# Revit family: 45120183
name_source: partatom
category: Plumbing Fixtures
revit_build: Autodesk Revit 2018 (Build: 20170223_1515(x64)
units: mm (PartAtom-declared; Revit-internal decimal feet)

## family parameters
Always vertical = Yes
Cut with Voids When Loaded = No
OmniClass Number = 23.45.55.00
OmniClass Title = Sanitary Faucets, Wastes
Part Type = Normal
Room Calculation Point = No
Round Connector Dimension = Use Diameter
Shared = No
Work Plane-Based = No

## types (1)
- 45120183 Shower faucet
    2D/3D/BIM Files URL = http://static.hansa.com
    3D View = https://static.hansa.com
    Additional Features = protected against back-flow in domestic use (according to DIN EN 1717)
    Advanced Features = Inner body made of DZR brass
    Approval DVGW = DW-6506CS0561
    Approval KIWA = K6116/08
    AssetType = Fixed
    BIMObjectName = 45120183
    Backflow Prevention EN1717 = EB
    BodyMaterial = Brass
    Brand = HANSA
    Catalog Drawing URL = http://static.hansa.com
    Category = Bathroom;Shower
    CloseOffRating = 0
    Color = Chrome
    Connection = Eccentric coupling(s)
    Dimension Drawing URL = http://static.hansa.com
    DurationUnit = Year
    EAN Number = 4057304003011
    EN Standard = EN 817
    ETIM Class Number = EC011329 Shower mixing tap
    FDV Document URL = http://www.hansa.com
    FaucetMainMaterial = Brass
    Features = Single-lever
    Finish = Polished
    Flow Drawing URL = http://static.hansa.com
    Flow Rate At 300kPa = 0.3 L/s
    FlowCoefficient = 0
    Group = Shower faucet
    HWFU = 0
    IfcExportAs = IfcValveType
    IfcExportType = FAUCET
    Installation Type = Wall mounted
    Installation and Maintenance Guide URL = http://static.hansa.com
    Interactive AR View URL = https://static.hansa.com
    Lever Handle = Hot/Cold symbols;Single operating lever/handle
    Manufacturer = HANSA
    ManufacturerName = HANSA
    ManufacturerURL = http://www.hansa.com
    Market = Austria;Belgium;Czech Republic;Germany;Spain;France;International;Italy;Netherlands;Slovakia
    Material = Brass
    Max. Hot Water Supply = 80 °C
    Mechanical Parts = Non-return valve(s);ø 40 mm ceramic cartridge for flow and temperature control
    Mobile Product Information URL = http://mpi.hansa.com
    Model = 45120183 Shower faucet
    ModelReference = 45120183
    NBSDescription = Shower mixers
    NBSReference = 45-35-70/335
    Name = 45120183 Shower faucet
    Name_en = 45120183 Shower faucet
    NominalDepth = 207 mm
    NominalHeight = 106 mm
    NominalWidth = 220 mm
    Product Code = 45120183
    Product Family = HANSAPINTO
    Product Image URL = http://static.hansa.com
    Product URL = http://static.hansa.com
    Revision = 4
    Sales Package dimensions (LxWxH) = 200 x 165 x 95
    Shape = Sculptured
    Size = 220x207x106 mm
    Spare-Part Information URL = http://static.hansa.com
    Surface treatment = Chrome
    Technical DataSheet URL = http://www.hansa.com
    Temperature = THERMO COOL;Temperature limiter
    Temperature Adjustments = The housing of the fittings conducts minimal heat;Limitation option for maximum temperature and flow-rate ;Adjustable hot water stop (included, retrofittable)
    UNSPSC Class Number = 30181700 Faucets or taps
    URL DVGW = http://static.hansa.com
    URL Declaration of Conformity = http://static.hansa.com
    URL KIWA = http://static.hansa.com
    URL REACH = http://static.hansa.com
    Uniclass2 = Pr_40_30_96_78
    Uniclass2015Description = Shower manual water supply sets
    Uniclass2015Reference = Pr_40_20_87_78
    Version = 4
    VersionDate = 01/07/2022
    Warranty Information URL = http://warranty.hansa.com
    WarrantyDescription = http://warranty.hansa.com
    WarrantyDurationUnit = Year
    Working Pressure = 50 - 1000 kPa
    WorkingPressure = 50 - 1000 kPa

## geometry (parser evidence)
native form markers: Sweep x3
no freeform markers — native parametric forms only
